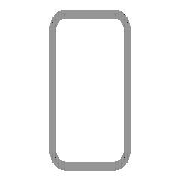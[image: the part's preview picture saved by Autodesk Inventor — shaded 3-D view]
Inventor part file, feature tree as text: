
AUTODESK INVENTOR PART (.ipt)
format: ipt  version: 2025 (Build 290162010, 162A)  size: 150,016 bytes
history: native  units: mm (DEFAULTED — no unit token found)
features: other x4, sketch x2, extrude x1, plane x1
ambient origin geometry x8: Origin, YZ Plane, XZ Plane, XY Plane, X Axis, Y Axis, Z Axis, Center Point
bodies: Solid1 (feature_tree), Body (feature_tree)
feature tree (8):
  parser-record x1  (decoder bookkeeping rows leaked as tree rows — omitted from the tree; the rows remain in map.json)
  other  "Driven Length"
  other  "Start Plane"
  other  "End Plane"
  extrude  "Extrusion2"  TaperAngle=0.0deg  [1 undecoded]
  sketch  "Sketch3"  dims[d3=2881.0mm d4=0.0mm]
  plane  "Work Plane3"
  sketch  "Sketch5"  dims[d7=6.0mm d9=20.0mm d11=40.0mm d12=3.0mm d13=-0.0mm d14=2881.0mm d15=10.0mm d16=20.0mm d17=90.0deg d18=2881.0mm d19=6.747443mm d20=0.0mm d21=0.0mm]
note: 1 required parameter value undecoded (feature->parameter linkage not recoverable at this tier; creation-order binding heuristic only, values carry confidence <= 0.55)
